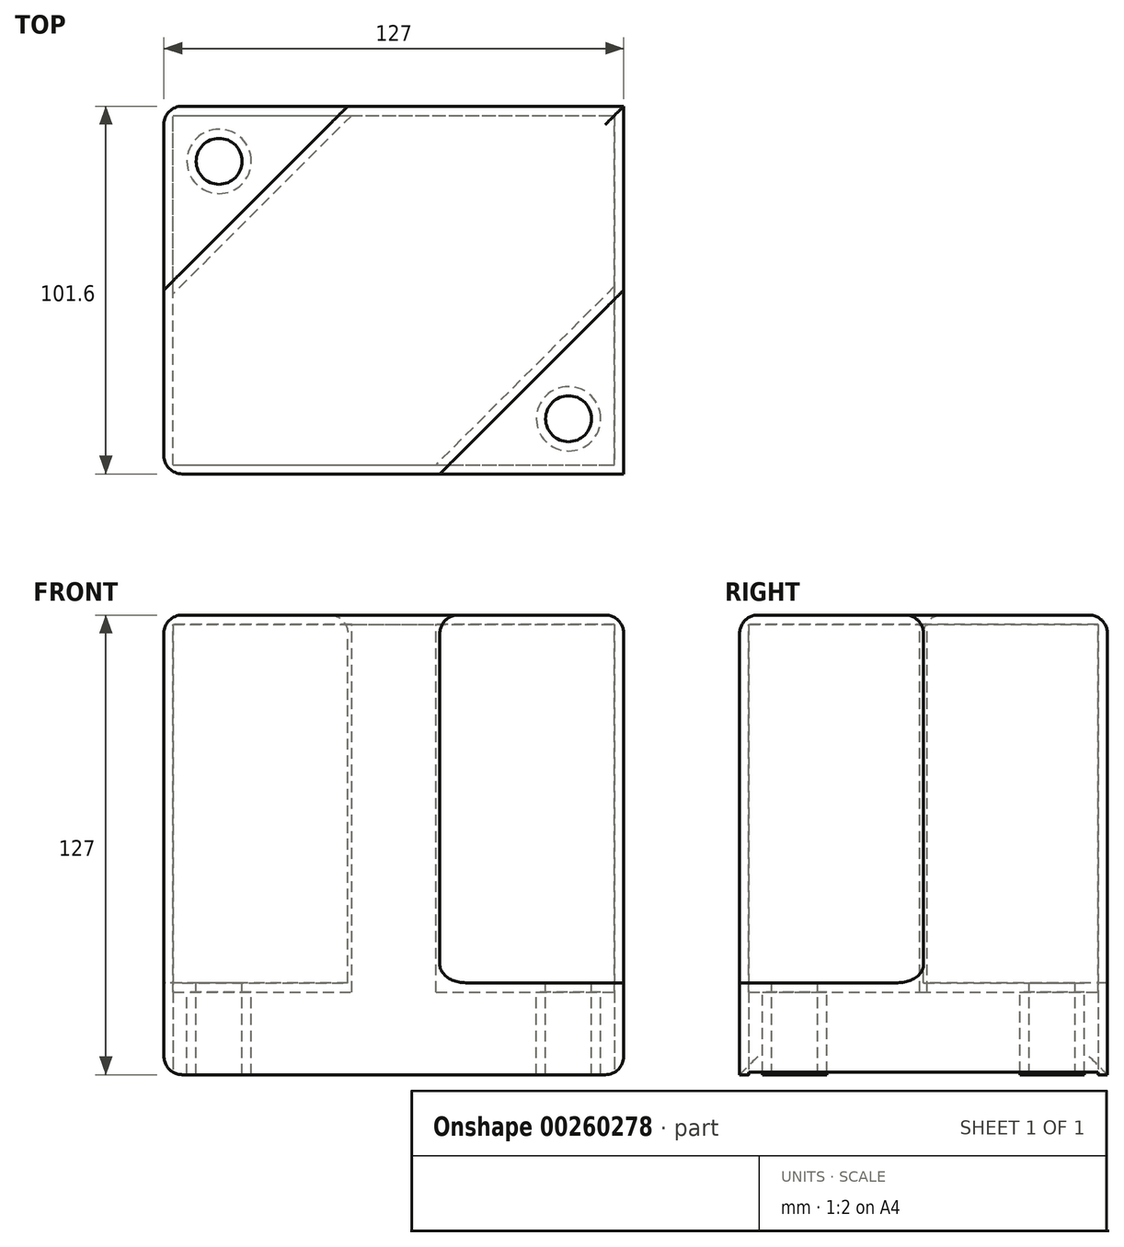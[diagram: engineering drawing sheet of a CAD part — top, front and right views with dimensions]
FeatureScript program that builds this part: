
annotation { "Feature Type Name" : "Feature", "Feature Type Description" : "" }
export const myFeature = defineFeature(function(context is Context, id is Id, definition is map)
    precondition{}
    {
        {
            var Q0;
            Q0=qCreatedBy(makeId("Front.planeOp"),FACE);
            var sketch = newSketch(context, id + "F0", { "sketchPlane" : qUnion([Q0])});
            skLineSegment(sketch, "E0.bottom", {"start": v(-65.48, 93.55) * mm, "end": v(61.52, 93.55) * mm});
            skLineSegment(sketch, "E0.top", {"start": v(-65.48, -33.45) * mm, "end": v(61.52, -33.45) * mm});
            skLineSegment(sketch, "E0.left", {"start": v(-65.48, 93.55) * mm, "end": v(-65.48, -33.45) * mm});
            skLineSegment(sketch, "E0.right", {"start": v(61.52, 93.55) * mm, "end": v(61.52, -33.45) * mm});
            skSolve(sketch);
        }
        {
            var Q0;
            Q0=makeQuery(id+"F0.imprint","IMPRINT",FACE,{"disambiguationData":[TD([[makeQuery(id+"F0.imprint","IMPRINT",EDGE,{"derivedFrom":sQuery(id+"F0.wireOp",EDGE,"E0.bottom")}),-1.0]])]});
            extrude(context, id + "F1", {"entities" : qUnion([Q0]), "depth" : 101.6 * mm});
        }
        {
            var Q0;
            Q0=makeQuery(id+"F1.opExtrude","SWEPT_FACE",FACE,{"disambiguationData":[OSD([sQuery(id+"F0.wireOp",EDGE,"E0.bottom")])]});
            var sketch = newSketch(context, id + "F2", { "sketchPlane" : qUnion([Q0])});
            skLineSegment(sketch, "E1", {"start": v(61.52, -101.6) * mm, "end": v(61.52, -50.8) * mm});
            skLineSegment(sketch, "E2", {"start": v(61.52, -50.8) * mm, "end": v(10.72, -101.6) * mm});
            skLineSegment(sketch, "E3", {"start": v(10.72, -101.6) * mm, "end": v(61.52, -101.6) * mm});
            skLineSegment(sketch, "E4", {"start": v(-65.48, 0) * mm, "end": v(-14.68, 0) * mm});
            skLineSegment(sketch, "E5", {"start": v(-14.68, 0) * mm, "end": v(-65.48, -50.8) * mm});
            skLineSegment(sketch, "E6", {"start": v(-65.48, -50.8) * mm, "end": v(-65.48, 0) * mm});
            skSolve(sketch);
        }
        {
            var Q0;
            Q0=makeQuery(id+"F2.imprint","IMPRINT",FACE,{"disambiguationData":[TD([[makeQuery(id+"F2.imprint","IMPRINT",EDGE,{"derivedFrom":sQuery(id+"F2.wireOp",EDGE,"E4")}),-1.0]])]});
            var Q1;
            Q1=makeQuery(id+"F2.imprint","IMPRINT",FACE,{"disambiguationData":[TD([[makeQuery(id+"F2.imprint","IMPRINT",EDGE,{"derivedFrom":sQuery(id+"F2.wireOp",EDGE,"E1")}),1.0]])]});
            extrude(context, id + "F3", {"entities" : qUnion([Q0, Q1]), "operationType" : NewBodyOperationType.REMOVE, "oppositeDirection" : true, "depth" : 101.6 * mm});
        }
        {
            var Q0;
            Q0=makeQuery(id+"F3.boolean.opBoolean","COPY",FACE,{"derivedFrom":makeQuery(id+"F3.opExtrude","CAP_FACE",FACE,{"disambiguationData":[OSD([sQuery(id+"F2.wireOp",EDGE,"E4"),sQuery(id+"F2.wireOp",EDGE,"E5"),sQuery(id+"F2.wireOp",EDGE,"E6")])],"isStart":false})});
            var sketch = newSketch(context, id + "F4", { "sketchPlane" : qUnion([Q0])});
            skCircle(sketch, "E7", {"center": v(-50.24, -15.24) * mm, "radius": 6.35 * mm});
            skCircle(sketch, "E8", {"center": v(46.28, -86.36) * mm, "radius": 6.35 * mm});
            skSolve(sketch);
        }
        {
            var Q0;
            Q0=makeQuery(id+"F4.imprint","IMPRINT",FACE,{"disambiguationData":[TD([[makeQuery(id+"F4.imprint","IMPRINT",EDGE,{"derivedFrom":sQuery(id+"F4.wireOp",EDGE,"E7")}),1.0]])]});
            var Q1;
            Q1=makeQuery(id+"F4.imprint","IMPRINT",FACE,{"disambiguationData":[TD([[makeQuery(id+"F4.imprint","IMPRINT",EDGE,{"derivedFrom":sQuery(id+"F4.wireOp",EDGE,"E8")}),1.0]])]});
            extrude(context, id + "F5", {"entities" : qUnion([Q0, Q1]), "operationType" : NewBodyOperationType.REMOVE, "oppositeDirection" : true, "depth" : 203.2 * mm});
        }
        {
            var Q0;
            Q0=makeQuery(id+"F1.opExtrude","SWEPT_FACE",FACE,{"disambiguationData":[OSD([sQuery(id+"F0.wireOp",EDGE,"E0.top")])]});
            shell(context, id + "F6", {"entities" : qUnion([Q0]), "thickness" : 2.54 * mm});
        }
        {
            var Q0;
            Q0=makeQuery(id+"F3.boolean.opBoolean","COPY",EDGE,{"derivedFrom":makeQuery(id+"F3.opExtrude","CAP_EDGE",EDGE,{"disambiguationData":[OSD([sQuery(id+"F2.wireOp",EDGE,"E2")])],"isStart":true})});
            var Q1;
            Q1=makeQuery(id+"F1.opExtrude","CAP_EDGE",EDGE,{"disambiguationData":[OSD([sQuery(id+"F0.wireOp",EDGE,"E0.bottom")])],"isStart":false});
            var Q2;
            Q2=makeQuery(id+"F1.opExtrude","SWEPT_EDGE",EDGE,{"disambiguationData":[OSD([sQuery(id+"F0.wireOp",EDGE,"E0.bottom"),sQuery(id+"F0.wireOp",EDGE,"E0.left")])]});
            var Q3;
            Q3=makeQuery(id+"F3.boolean.opBoolean","COPY",EDGE,{"derivedFrom":makeQuery(id+"F3.opExtrude","CAP_EDGE",EDGE,{"disambiguationData":[OSD([sQuery(id+"F2.wireOp",EDGE,"E5")])],"isStart":true})});
            var Q4;
            Q4=makeQuery(id+"F1.opExtrude","CAP_EDGE",EDGE,{"disambiguationData":[OSD([sQuery(id+"F0.wireOp",EDGE,"E0.bottom")])],"isStart":true});
            var Q5;
            Q5=makeQuery(id+"F1.opExtrude","SWEPT_EDGE",EDGE,{"disambiguationData":[OSD([sQuery(id+"F0.wireOp",EDGE,"E0.bottom"),sQuery(id+"F0.wireOp",EDGE,"E0.right")])]});
            var Q6;
            Q6=makeQuery(id+"F1.opExtrude","CAP_EDGE",EDGE,{"disambiguationData":[OSD([sQuery(id+"F0.wireOp",EDGE,"E0.left")])],"isStart":false});
            var Q7;
            Q7=makeQuery(id+"F3.boolean.opBoolean","COPY",EDGE,{"derivedFrom":makeQuery(id+"F3.opExtrude","SWEPT_EDGE",EDGE,{"disambiguationData":[OSD([sQuery(id+"F0.wireOp",EDGE,"E0.bottom"),sQuery(id+"F2.wireOp",EDGE,"E2"),sQuery(id+"F2.wireOp",EDGE,"E3")])]})});
            var Q8;
            Q8=makeQuery(id+"F3.boolean.opBoolean","COPY",EDGE,{"derivedFrom":makeQuery(id+"F3.opExtrude","SWEPT_EDGE",EDGE,{"disambiguationData":[OSD([sQuery(id+"F0.wireOp",EDGE,"E0.bottom"),sQuery(id+"F0.wireOp",EDGE,"E0.right"),sQuery(id+"F2.wireOp",EDGE,"E1"),sQuery(id+"F2.wireOp",EDGE,"E2")])]})});
            var Q9;
            Q9=makeQuery(id+"F3.boolean.opBoolean","COPY",EDGE,{"derivedFrom":makeQuery(id+"F3.opExtrude","CAP_EDGE",EDGE,{"disambiguationData":[OSD([sQuery(id+"F2.wireOp",EDGE,"E1")])],"isStart":false})});
            var Q10;
            Q10=makeQuery(id+"F3.boolean.opBoolean","COPY",EDGE,{"derivedFrom":makeQuery(id+"F3.opExtrude","CAP_EDGE",EDGE,{"disambiguationData":[OSD([sQuery(id+"F2.wireOp",EDGE,"E3")])],"isStart":false})});
            var Q11;
            Q11=makeQuery(id+"F3.boolean.opBoolean","COPY",EDGE,{"derivedFrom":makeQuery(id+"F3.opExtrude","CAP_EDGE",EDGE,{"disambiguationData":[OSD([sQuery(id+"F2.wireOp",EDGE,"E2")])],"isStart":false})});
            var Q12;
            Q12=makeQuery(id+"F1.opExtrude","SWEPT_EDGE",EDGE,{"disambiguationData":[OSD([sQuery(id+"F0.wireOp",EDGE,"E0.top"),sQuery(id+"F0.wireOp",EDGE,"E0.right")])]});
            var Q13;
            Q13=makeQuery(id+"F3.boolean.opBoolean","COPY",EDGE,{"derivedFrom":makeQuery(id+"F3.opExtrude","SWEPT_EDGE",EDGE,{"disambiguationData":[OSD([sQuery(id+"F0.wireOp",EDGE,"E0.bottom"),sQuery(id+"F0.wireOp",EDGE,"E0.left"),sQuery(id+"F2.wireOp",EDGE,"E5"),sQuery(id+"F2.wireOp",EDGE,"E6")])]})});
            var Q14;
            Q14=makeQuery(id+"F3.boolean.opBoolean","COPY",EDGE,{"derivedFrom":makeQuery(id+"F3.opExtrude","CAP_EDGE",EDGE,{"disambiguationData":[OSD([sQuery(id+"F2.wireOp",EDGE,"E6")])],"isStart":false})});
            var Q15;
            Q15=makeQuery(id+"F1.opExtrude","CAP_EDGE",EDGE,{"disambiguationData":[OSD([sQuery(id+"F0.wireOp",EDGE,"E0.left")])],"isStart":true});
            var Q16;
            Q16=makeQuery(id+"F1.opExtrude","SWEPT_EDGE",EDGE,{"disambiguationData":[OSD([sQuery(id+"F0.wireOp",EDGE,"E0.top"),sQuery(id+"F0.wireOp",EDGE,"E0.left")])]});
            var Q17;
            Q17=makeQuery(id+"F3.boolean.opBoolean","COPY",EDGE,{"derivedFrom":makeQuery(id+"F3.opExtrude","CAP_EDGE",EDGE,{"disambiguationData":[OSD([sQuery(id+"F2.wireOp",EDGE,"E4")])],"isStart":false})});
            var Q18;
            Q18=makeQuery(id+"F3.boolean.opBoolean","COPY",EDGE,{"derivedFrom":makeQuery(id+"F3.opExtrude","SWEPT_EDGE",EDGE,{"disambiguationData":[OSD([sQuery(id+"F0.wireOp",EDGE,"E0.bottom"),sQuery(id+"F2.wireOp",EDGE,"E4"),sQuery(id+"F2.wireOp",EDGE,"E5")])]})});
            fillet(context, id + "F7", {"entities" : qUnion([Q0, Q1, Q2, Q3, Q4, Q5, Q6, Q7, Q8, Q9, Q10, Q11, Q12, Q13, Q14, Q15, Q16, Q17, Q18]), "radius" : 5.08 * mm, "tangentPropagation" : true, "allowEdgeOverflow" : false});
        }
    });
